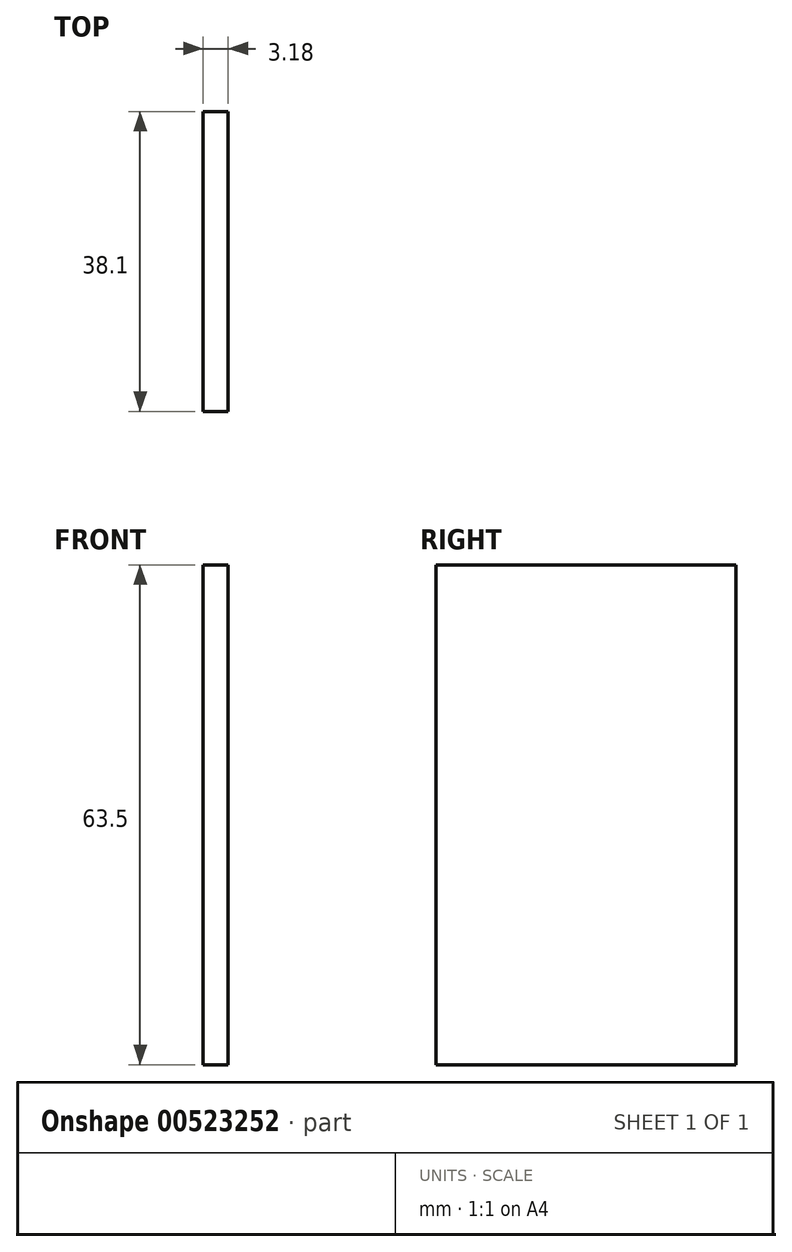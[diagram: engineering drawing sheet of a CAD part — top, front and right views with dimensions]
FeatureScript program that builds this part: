
annotation { "Feature Type Name" : "Feature", "Feature Type Description" : "" }
export const myFeature = defineFeature(function(context is Context, id is Id, definition is map)
    precondition{}
    {
        {
            var Q0;
            Q0=qCreatedBy(makeId("Front.planeOp"),FACE);
            var sketch = newSketch(context, id + "F0", { "sketchPlane" : qUnion([Q0])});
            skLineSegment(sketch, "E0", {"start": v(-62.46, -18.21) * mm, "end": v(-62.46, 45.29) * mm});
            skLineSegment(sketch, "E1", {"start": v(-62.46, 45.29) * mm, "end": v(-59.28, 45.29) * mm});
            skLineSegment(sketch, "E2", {"start": v(-62.46, -18.21) * mm, "end": v(-59.28, -18.21) * mm});
            skLineSegment(sketch, "E3", {"start": v(-59.28, -18.21) * mm, "end": v(-59.28, 45.29) * mm});
            skSolve(sketch);
        }
        {
            var Q0;
            Q0 = qSketchRegion(id + "F0", true);
            extrude(context, id + "F1", {"entities" : qUnion([Q0]), "depth" : 38.1 * mm, "offsetDistance" : 25.4 * mm});
        }
    });
